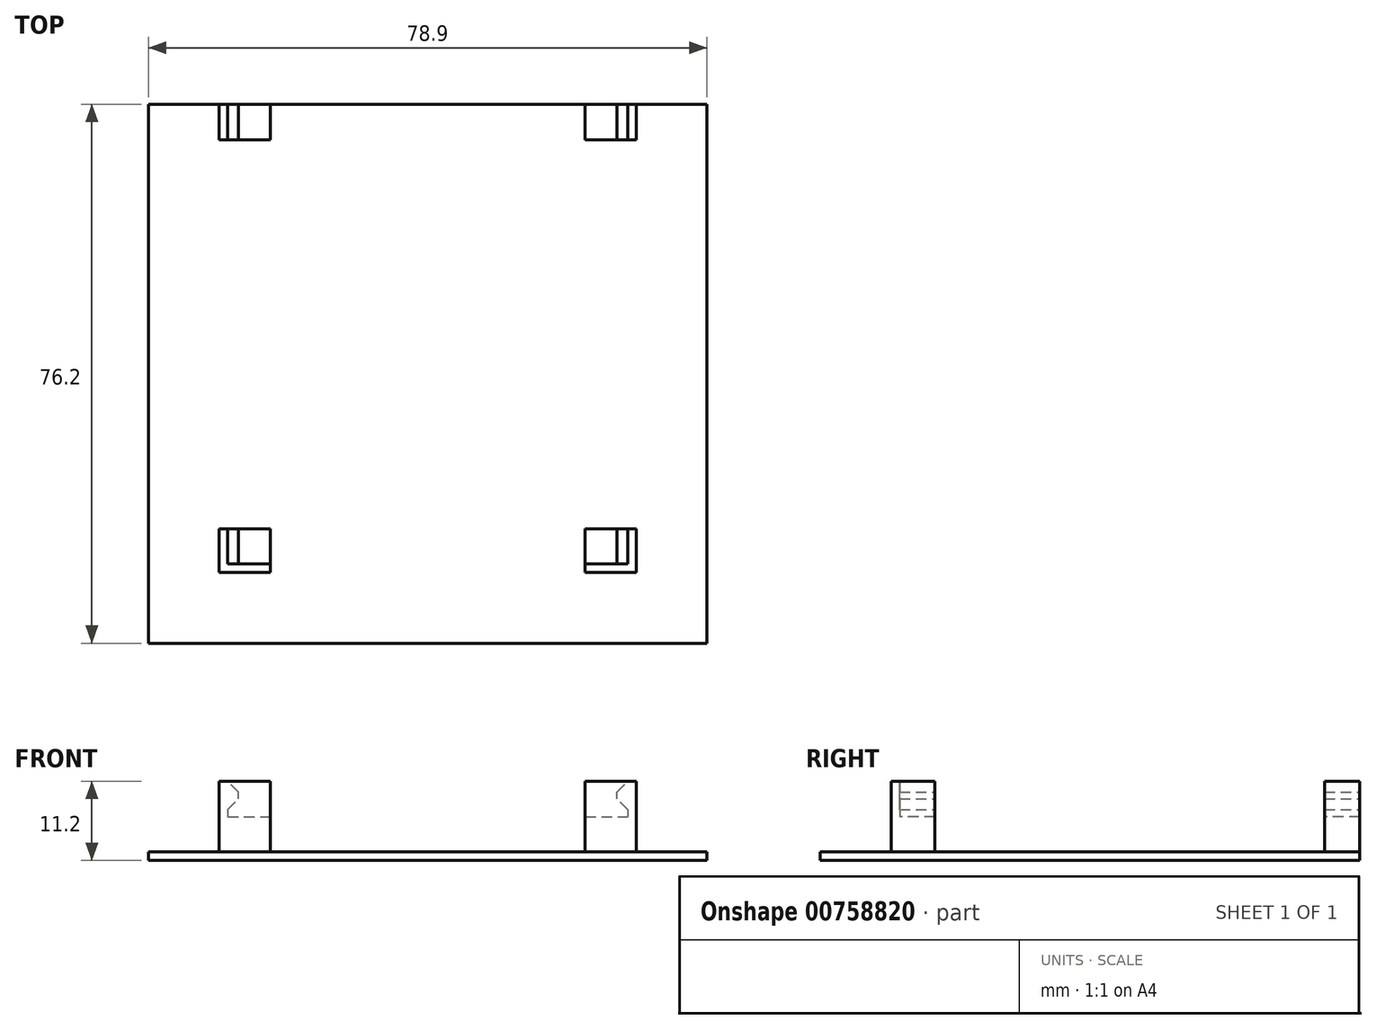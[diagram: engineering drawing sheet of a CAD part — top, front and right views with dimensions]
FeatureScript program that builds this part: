
annotation { "Feature Type Name" : "Feature", "Feature Type Description" : "" }
export const myFeature = defineFeature(function(context is Context, id is Id, definition is map)
    precondition{}
    {
        {
            var Q0;
            Q0=qCreatedBy(makeId("Top.planeOp"),FACE);
            var sketch = newSketch(context, id + "F0", { "sketchPlane" : qUnion([Q0])});
            skLineSegment(sketch, "E0.bottom", {"start": v(0, 0) * mm, "end": v(78.9, 0) * mm});
            skLineSegment(sketch, "E0.top", {"start": v(0, -76.2) * mm, "end": v(78.9, -76.2) * mm});
            skLineSegment(sketch, "E0.left", {"start": v(0, 0) * mm, "end": v(0, -76.2) * mm});
            skLineSegment(sketch, "E0.right", {"start": v(78.9, 0) * mm, "end": v(78.9, -76.2) * mm});
            skLineSegment(sketch, "E1.bottom", {"start": v(11.2, 0) * mm, "end": v(17.2, 0) * mm});
            skLineSegment(sketch, "E1.top", {"start": v(11.2, -5) * mm, "end": v(17.2, -5) * mm});
            skLineSegment(sketch, "E1.left", {"start": v(11.2, 0) * mm, "end": v(11.2, -5) * mm});
            skLineSegment(sketch, "E1.right", {"start": v(17.2, 0) * mm, "end": v(17.2, -5) * mm});
            skLineSegment(sketch, "E2.bottom", {"start": v(61.7, 0) * mm, "end": v(67.7, 0) * mm});
            skLineSegment(sketch, "E2.top", {"start": v(61.7, -5) * mm, "end": v(67.7, -5) * mm});
            skLineSegment(sketch, "E2.left", {"start": v(61.7, 0) * mm, "end": v(61.7, -5) * mm});
            skLineSegment(sketch, "E2.right", {"start": v(67.7, 0) * mm, "end": v(67.7, -5) * mm});
            skLineSegment(sketch, "E3.bottom", {"start": v(11.2, -60) * mm, "end": v(17.2, -60) * mm});
            skLineSegment(sketch, "E3.top", {"start": v(11.2, -65) * mm, "end": v(17.2, -65) * mm});
            skLineSegment(sketch, "E3.left", {"start": v(11.2, -60) * mm, "end": v(11.2, -65) * mm});
            skLineSegment(sketch, "E3.right", {"start": v(17.2, -60) * mm, "end": v(17.2, -65) * mm});
            skLineSegment(sketch, "E4.bottom", {"start": v(61.7, -60) * mm, "end": v(67.7, -60) * mm});
            skLineSegment(sketch, "E4.top", {"start": v(61.7, -65) * mm, "end": v(67.7, -65) * mm});
            skLineSegment(sketch, "E4.left", {"start": v(61.7, -60) * mm, "end": v(61.7, -65) * mm});
            skLineSegment(sketch, "E4.right", {"start": v(67.7, -60) * mm, "end": v(67.7, -65) * mm});
            skLineSegment(sketch, "E5", {"start": v(11.2, -60) * mm, "end": v(10, -60) * mm});
            skLineSegment(sketch, "E6", {"start": v(10, -60) * mm, "end": v(10, -66.2) * mm});
            skLineSegment(sketch, "E7", {"start": v(10, -66.2) * mm, "end": v(17.2, -66.2) * mm});
            skLineSegment(sketch, "E8", {"start": v(17.2, -66.2) * mm, "end": v(17.2, -65) * mm});
            skLineSegment(sketch, "E9", {"start": v(61.7, -65) * mm, "end": v(61.7, -66.2) * mm});
            skLineSegment(sketch, "E10", {"start": v(61.7, -66.2) * mm, "end": v(68.9, -66.2) * mm});
            skLineSegment(sketch, "E11", {"start": v(68.9, -66.2) * mm, "end": v(68.9, -60) * mm});
            skLineSegment(sketch, "E12", {"start": v(68.9, -60) * mm, "end": v(67.7, -60) * mm});
            skLineSegment(sketch, "E13.bottom", {"start": v(11.2, 0) * mm, "end": v(10, 0) * mm});
            skLineSegment(sketch, "E13.top", {"start": v(11.2, -5) * mm, "end": v(10, -5) * mm});
            skLineSegment(sketch, "E13.right", {"start": v(10, 0) * mm, "end": v(10, -5) * mm});
            skLineSegment(sketch, "E14.bottom", {"start": v(67.7, 0) * mm, "end": v(68.9, 0) * mm});
            skLineSegment(sketch, "E14.top", {"start": v(67.7, -5) * mm, "end": v(68.9, -5) * mm});
            skLineSegment(sketch, "E14.right", {"start": v(68.9, 0) * mm, "end": v(68.9, -5) * mm});
            skSolve(sketch);
        }
        {
            var Q0;
            Q0=makeQuery(id+"F0.imprint","IMPRINT",FACE,{"disambiguationData":[TD([[makeQuery(id+"F0.imprint","IMPRINT",EDGE,{"derivedFrom":sQuery(id+"F0.wireOp",EDGE,"E1.top")}),1.0]])]});
            var Q1;
            {var subQ0=sQuery(id+"F0.wireOp",EDGE,"E1.left");Q1=makeQuery(id+"F0.imprint","IMPRINT",FACE,{"disambiguationData":[TD([[makeQuery(id+"F0.imprint","IMPRINT",EDGE,{"derivedFrom":subQ0}),-1.0]])]});}
            var Q2;
            Q2=makeQuery(id+"F0.imprint","IMPRINT",FACE,{"disambiguationData":[TD([[makeQuery(id+"F0.imprint","IMPRINT",EDGE,{"derivedFrom":sQuery(id+"F0.wireOp",EDGE,"E0.top")}),1.0]])]});
            var Q3;
            Q3=makeQuery(id+"F0.imprint","IMPRINT",FACE,{"disambiguationData":[TD([[makeQuery(id+"F0.imprint","IMPRINT",EDGE,{"derivedFrom":sQuery(id+"F0.wireOp",EDGE,"E2.top")}),1.0]])]});
            var Q4;
            {var subQ0=sQuery(id+"F0.wireOp",EDGE,"E2.right");Q4=makeQuery(id+"F0.imprint","IMPRINT",FACE,{"disambiguationData":[TD([[makeQuery(id+"F0.imprint","IMPRINT",EDGE,{"derivedFrom":subQ0}),1.0]])]});}
            var Q5;
            Q5=makeQuery(id+"F0.imprint","IMPRINT",FACE,{"disambiguationData":[TD([[makeQuery(id+"F0.imprint","IMPRINT",EDGE,{"derivedFrom":sQuery(id+"F0.wireOp",EDGE,"E4.bottom")}),-1.0]])]});
            var Q6;
            Q6=makeQuery(id+"F0.imprint","IMPRINT",FACE,{"disambiguationData":[TD([[makeQuery(id+"F0.imprint","IMPRINT",EDGE,{"derivedFrom":sQuery(id+"F0.wireOp",EDGE,"E4.top")}),-1.0]])]});
            var Q7;
            Q7=makeQuery(id+"F0.imprint","IMPRINT",FACE,{"disambiguationData":[TD([[makeQuery(id+"F0.imprint","IMPRINT",EDGE,{"derivedFrom":sQuery(id+"F0.wireOp",EDGE,"E3.bottom")}),-1.0]])]});
            var Q8;
            Q8=makeQuery(id+"F0.imprint","IMPRINT",FACE,{"disambiguationData":[TD([[makeQuery(id+"F0.imprint","IMPRINT",EDGE,{"derivedFrom":sQuery(id+"F0.wireOp",EDGE,"E3.top")}),-1.0]])]});
            extrude(context, id + "F1", {"entities" : qUnion([Q0, Q1, Q2, Q3, Q4, Q5, Q6, Q7, Q8]), "oppositeDirection" : true, "depth" : 1.2 * mm, "offsetDistance" : 25 * mm});
        }
        {
            var Q0;
            Q0=makeQuery(id+"F0.imprint","IMPRINT",FACE,{"disambiguationData":[TD([[makeQuery(id+"F0.imprint","IMPRINT",EDGE,{"derivedFrom":sQuery(id+"F0.wireOp",EDGE,"E1.top")}),1.0]])]});
            var Q1;
            Q1=makeQuery(id+"F0.imprint","IMPRINT",FACE,{"disambiguationData":[TD([[makeQuery(id+"F0.imprint","IMPRINT",EDGE,{"derivedFrom":sQuery(id+"F0.wireOp",EDGE,"E3.bottom")}),-1.0]])]});
            var Q2;
            Q2=makeQuery(id+"F0.imprint","IMPRINT",FACE,{"disambiguationData":[TD([[makeQuery(id+"F0.imprint","IMPRINT",EDGE,{"derivedFrom":sQuery(id+"F0.wireOp",EDGE,"E2.top")}),1.0]])]});
            var Q3;
            Q3=makeQuery(id+"F0.imprint","IMPRINT",FACE,{"disambiguationData":[TD([[makeQuery(id+"F0.imprint","IMPRINT",EDGE,{"derivedFrom":sQuery(id+"F0.wireOp",EDGE,"E4.bottom")}),-1.0]])]});
            extrude(context, id + "F2", {"entities" : qUnion([Q0, Q1, Q2, Q3]), "operationType" : NewBodyOperationType.ADD, "depth" : 5 * mm, "offsetDistance" : 25 * mm});
        }
        {
            var Q0;
            Q0=makeQuery(id+"F0.imprint","IMPRINT",FACE,{"disambiguationData":[TD([[makeQuery(id+"F0.imprint","IMPRINT",EDGE,{"derivedFrom":sQuery(id+"F0.wireOp",EDGE,"E3.top")}),-1.0]])]});
            var Q1;
            Q1=makeQuery(id+"F0.imprint","IMPRINT",FACE,{"disambiguationData":[TD([[makeQuery(id+"F0.imprint","IMPRINT",EDGE,{"derivedFrom":sQuery(id+"F0.wireOp",EDGE,"E4.top")}),-1.0]])]});
            var Q2;
            {var subQ0=sQuery(id+"F0.wireOp",EDGE,"E2.right");Q2=makeQuery(id+"F0.imprint","IMPRINT",FACE,{"disambiguationData":[TD([[makeQuery(id+"F0.imprint","IMPRINT",EDGE,{"derivedFrom":subQ0}),1.0]])]});}
            var Q3;
            {var subQ0=sQuery(id+"F0.wireOp",EDGE,"E1.left");Q3=makeQuery(id+"F0.imprint","IMPRINT",FACE,{"disambiguationData":[TD([[makeQuery(id+"F0.imprint","IMPRINT",EDGE,{"derivedFrom":subQ0}),-1.0]])]});}
            extrude(context, id + "F3", {"entities" : qUnion([Q0, Q1, Q2, Q3]), "operationType" : NewBodyOperationType.ADD, "depth" : 10 * mm, "offsetDistance" : 25 * mm});
        }
        {
            var Q0;
            {var subQ0=sQuery(id+"F0.wireOp",EDGE,"E0.bottom");var subQ1=makeQuery(id+"F0.imprint","INTERSECT",VERTEX,{"derivedFrom":[subQ0,sQuery(id+"F0.wireOp",EDGE,"E1.left")]});var subQ2=makeQuery(id+"F0.imprint","INTERSECT",VERTEX,{"derivedFrom":[subQ0,sQuery(id+"F0.wireOp",EDGE,"E2.right")]});Q0=makeQuery(id+"F3.boolean.opBoolean","MERGE",FACE,{"derivedFrom":[makeQuery(id+"F2.boolean.opBoolean","MERGE",FACE,{"derivedFrom":[makeQuery(id+"F1.opExtrude","SWEPT_FACE",FACE,{"disambiguationData":[OSD([subQ0])]}),makeQuery(id+"F2.opExtrude","SWEPT_FACE",FACE,{"disambiguationData":[OSD([subQ0]),TDD([makeQuery(id+"F0.imprint","IMPRINT",EDGE,{"disambiguationData":[TD([[makeQuery(id+"F0.imprint","INTERSECT",VERTEX,{"derivedFrom":[subQ0,sQuery(id+"F0.wireOp",EDGE,"E2.left")]}),-1.0]])],"derivedFrom":subQ0})])]}),makeQuery(id+"F2.opExtrude","SWEPT_FACE",FACE,{"disambiguationData":[OSD([subQ0]),TDD([makeQuery(id+"F0.imprint","IMPRINT",EDGE,{"disambiguationData":[TD([[makeQuery(id+"F0.imprint","INTERSECT",VERTEX,{"derivedFrom":[subQ0,sQuery(id+"F0.wireOp",EDGE,"E1.right")]}),1.0]])],"derivedFrom":subQ0})])]})]}),makeQuery(id+"F3.opExtrude","SWEPT_FACE",FACE,{"disambiguationData":[OSD([subQ0]),TDD([makeQuery(id+"F0.imprint","IMPRINT",EDGE,{"disambiguationData":[TD([[subQ2,-1.0]])],"derivedFrom":subQ0})])]}),makeQuery(id+"F3.opExtrude","SWEPT_FACE",FACE,{"disambiguationData":[OSD([subQ0]),TDD([makeQuery(id+"F0.imprint","IMPRINT",EDGE,{"disambiguationData":[TD([[subQ1,1.0]])],"derivedFrom":subQ0})])]})]});}
            var sketch = newSketch(context, id + "F4", { "sketchPlane" : qUnion([Q0])});
            skLineSegment(sketch, "E15", {"start": v(-11.2, 10) * mm, "end": v(-12.7, 8.5) * mm});
            skLineSegment(sketch, "E16", {"start": v(-12.7, 8.5) * mm, "end": v(-12.7, 7.5) * mm});
            skLineSegment(sketch, "E17", {"start": v(-12.7, 7.5) * mm, "end": v(-11.2, 6) * mm});
            skLineSegment(sketch, "E18", {"start": v(-11.2, 6) * mm, "end": v(-11.2, 10) * mm});
            skLineSegment(sketch, "E19", {"start": v(-61.7, 0) * mm, "end": v(-17.2, 0) * mm, "construction": true});
            skLineSegment(sketch, "E20", {"start": v(-39.45, 0) * mm, "end": v(-39.45, 14.98) * mm, "construction": true});
            skLineSegment(sketch, "E21.MirrorCS", {"start": v(-66.2, 8.5) * mm, "end": v(-66.2, 7.5) * mm});
            skLineSegment(sketch, "E22.MirrorCS", {"start": v(-67.7, 6) * mm, "end": v(-67.7, 10) * mm});
            skLineSegment(sketch, "E23.MirrorCS", {"start": v(-67.7, 10) * mm, "end": v(-66.2, 8.5) * mm});
            skLineSegment(sketch, "E24.MirrorCS", {"start": v(-66.2, 7.5) * mm, "end": v(-67.7, 6) * mm});
            skSolve(sketch);
        }
        {
            var Q0;
            Q0 = qSketchRegion(id + "F4", true);
            var Q1;
            Q1=makeQuery(id+"F3.opExtrude","SWEPT_FACE",FACE,{"disambiguationData":[OSD([sQuery(id+"F0.wireOp",EDGE,"E3.top")])]});
            extrude(context, id + "F5", {"entities" : qUnion([Q0]), "operationType" : NewBodyOperationType.ADD, "endBound" : BoundingType.UP_TO_SURFACE, "oppositeDirection" : true, "depth" : 25 * mm, "endBoundEntityFace" : qUnion([Q1]), "offsetDistance" : 25 * mm});
        }
        {
            var Q0;
            Q0=makeQuery(id+"F0.imprint","IMPRINT",FACE,{"disambiguationData":[TD([[makeQuery(id+"F0.imprint","IMPRINT",EDGE,{"derivedFrom":sQuery(id+"F0.wireOp",EDGE,"E0.top")}),1.0]])]});
            var Q1;
            Q1=makeQuery(id+"F3.opExtrude","CAP_FACE",FACE,{"disambiguationData":[OSD([sQuery(id+"F0.wireOp",EDGE,"E0.bottom"),sQuery(id+"F0.wireOp",EDGE,"E1.left"),sQuery(id+"F0.wireOp",EDGE,"E13.top"),sQuery(id+"F0.wireOp",EDGE,"E13.right")])],"isStart":false});
            extrude(context, id + "F6", {"entities" : qUnion([Q0]), "operationType" : NewBodyOperationType.REMOVE, "endBound" : BoundingType.UP_TO_SURFACE, "depth" : 19.3 * mm, "endBoundEntityFace" : qUnion([Q1]), "offsetDistance" : 25 * mm});
        }
    });
